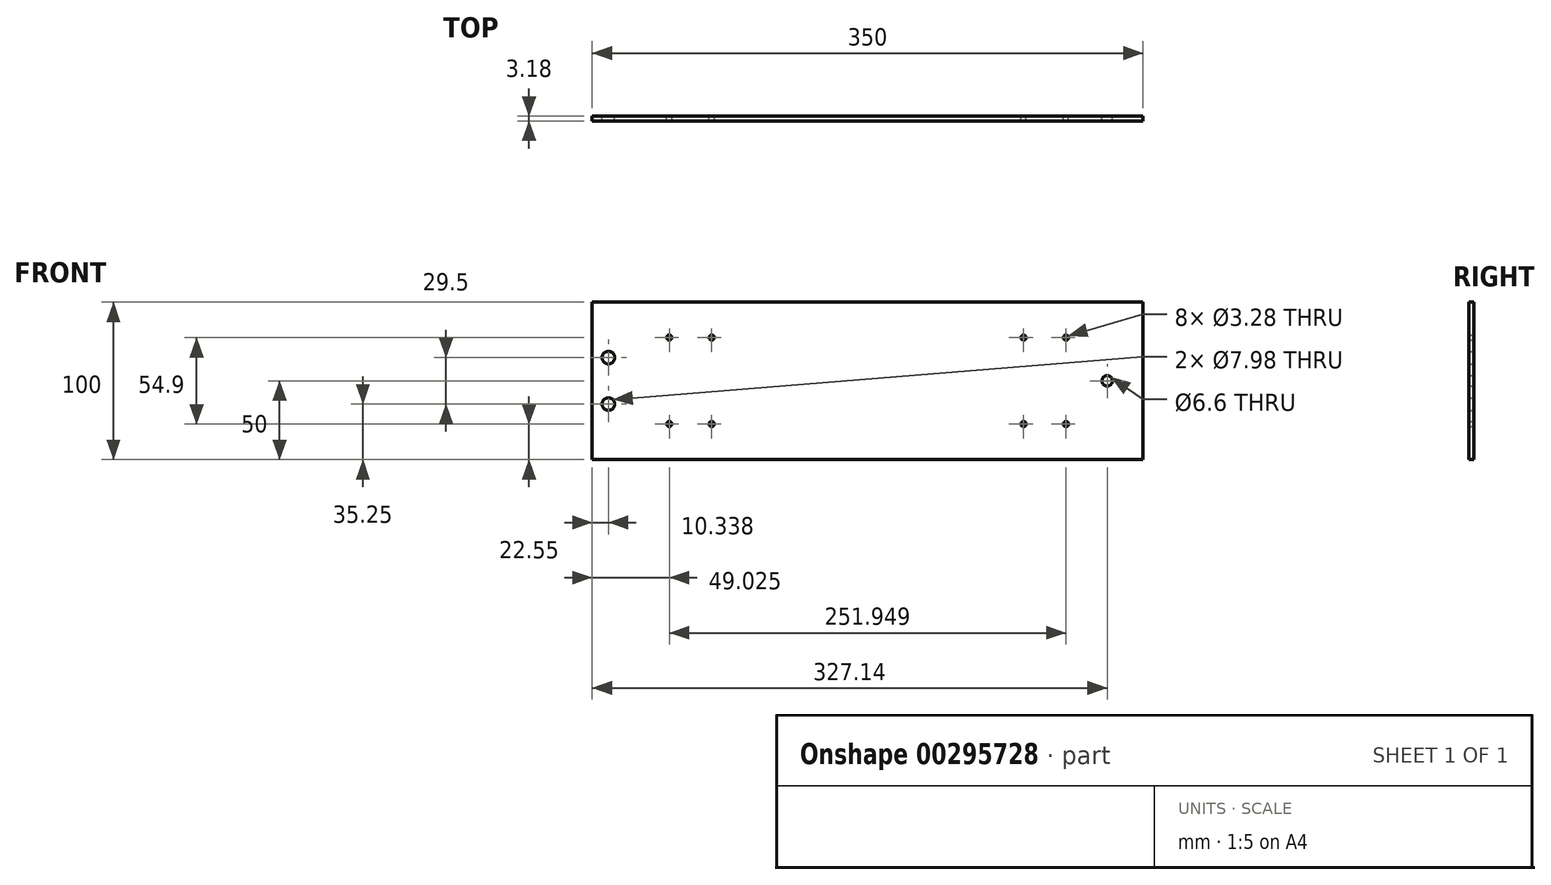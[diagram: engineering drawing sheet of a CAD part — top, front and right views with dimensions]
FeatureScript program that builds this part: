
annotation { "Feature Type Name" : "Feature", "Feature Type Description" : "" }
export const myFeature = defineFeature(function(context is Context, id is Id, definition is map)
    precondition{}
    {
        {
            var Q0;
            Q0=qCreatedBy(makeId("Front.planeOp"),FACE);
            var sketch = newSketch(context, id + "F0", { "sketchPlane" : qUnion([Q0])});
            skLineSegment(sketch, "E0.bottom", {"start": v(175, -75) * mm, "end": v(-175, -75) * mm});
            skLineSegment(sketch, "E0.top", {"start": v(175, 25) * mm, "end": v(-175, 25) * mm});
            skLineSegment(sketch, "E0.left", {"start": v(175, -75) * mm, "end": v(175, 25) * mm});
            skLineSegment(sketch, "E0.right", {"start": v(-175, -75) * mm, "end": v(-175, 25) * mm});
            skCircle(sketch, "E1", {"center": v(-112.5, 2.45) * mm, "radius": 4 * mm, "construction": true});
            skLineSegment(sketch, "E2", {"start": v(-112.5, 2.45) * mm, "end": v(-108.5, 2.45) * mm, "construction": true});
            skLineSegment(sketch, "E3", {"start": v(-112.5, 2.45) * mm, "end": v(-112.5, 6.45) * mm, "construction": true});
            skCircle(sketch, "E4", {"center": v(-99.03, 2.45) * mm, "radius": 1.64 * mm});
            skCircle(sketch, "E5.MirrorC", {"center": v(-125.97, 2.45) * mm, "radius": 1.64 * mm});
            skCircle(sketch, "E6", {"center": v(-112.5, -52.45) * mm, "radius": 4 * mm, "construction": true});
            skLineSegment(sketch, "E7", {"start": v(-112.5, -52.45) * mm, "end": v(-108.5, -52.45) * mm, "construction": true});
            skLineSegment(sketch, "E8", {"start": v(-112.5, -52.45) * mm, "end": v(-112.5, -48.45) * mm, "construction": true});
            skCircle(sketch, "E9", {"center": v(-99.03, -52.45) * mm, "radius": 1.64 * mm});
            skCircle(sketch, "E10.MirrorC", {"center": v(-125.97, -52.45) * mm, "radius": 1.64 * mm});
            skCircle(sketch, "E11", {"center": v(112.5, -52.45) * mm, "radius": 4 * mm, "construction": true});
            skLineSegment(sketch, "E12", {"start": v(112.5, -52.45) * mm, "end": v(116.5, -52.45) * mm, "construction": true});
            skLineSegment(sketch, "E13", {"start": v(112.5, -52.45) * mm, "end": v(112.5, -48.45) * mm, "construction": true});
            skCircle(sketch, "E14", {"center": v(125.97, -52.45) * mm, "radius": 1.64 * mm});
            skCircle(sketch, "E15.MirrorC", {"center": v(99.03, -52.45) * mm, "radius": 1.64 * mm});
            skCircle(sketch, "E16", {"center": v(112.5, 2.45) * mm, "radius": 4 * mm, "construction": true});
            skLineSegment(sketch, "E17", {"start": v(112.5, 2.45) * mm, "end": v(116.5, 2.45) * mm, "construction": true});
            skLineSegment(sketch, "E18", {"start": v(112.5, 2.45) * mm, "end": v(112.5, 6.45) * mm, "construction": true});
            skCircle(sketch, "E19", {"center": v(125.97, 2.45) * mm, "radius": 1.64 * mm});
            skCircle(sketch, "E20.MirrorC", {"center": v(99.03, 2.45) * mm, "radius": 1.64 * mm});
            skLineSegment(sketch, "E21.bottom", {"start": v(-74.4, -81.35) * mm, "end": v(-150.6, -81.35) * mm, "construction": true});
            skLineSegment(sketch, "E21.top", {"start": v(-74.4, -75) * mm, "end": v(-150.6, -75) * mm, "construction": true});
            skLineSegment(sketch, "E21.left", {"start": v(-74.4, -81.35) * mm, "end": v(-74.4, -75) * mm, "construction": true});
            skLineSegment(sketch, "E21.right", {"start": v(-150.6, -81.35) * mm, "end": v(-150.6, -75) * mm, "construction": true});
            skPoint(sketch, "E21.middle", {"position": v(-112.5, -78.17) * mm});
            skPoint(sketch, "E21.middle.positionSnap0", {"position": v(-112.5, -50.45) * mm});
            skPoint(sketch, "E21.centerSnap0", {"position": v(-112.5, -50.45) * mm});
            skLineSegment(sketch, "E22.bottom", {"start": v(-74.4, -75) * mm, "end": v(-49, -75) * mm, "construction": true});
            skLineSegment(sketch, "E22.top", {"start": v(-74.4, -81.35) * mm, "end": v(-49, -81.35) * mm, "construction": true});
            skLineSegment(sketch, "E22.left", {"start": v(-74.4, -75) * mm, "end": v(-74.4, -81.35) * mm, "construction": true});
            skLineSegment(sketch, "E22.right", {"start": v(-49, -75) * mm, "end": v(-49, -81.35) * mm, "construction": true});
            skLineSegment(sketch, "E23", {"start": v(-61.7, -75) * mm, "end": v(-61.7, -81.35) * mm, "construction": true});
            skLineSegment(sketch, "E24.MirrorCS", {"start": v(-74.4, 75) * mm, "end": v(-49, 75) * mm, "construction": true});
            skPoint(sketch, "E25.endSnap0", {"position": v(112.5, 0) * mm});
            skLineSegment(sketch, "E26.right", {"start": v(131.55, -7.94) * mm, "end": v(131.55, 7.94) * mm});
            skCircle(sketch, "E27", {"center": v(152.14, -25) * mm, "radius": 3.3 * mm});
            skCircle(sketch, "E28", {"center": v(-164.66, -39.75) * mm, "radius": 3.99 * mm});
            skLineSegment(sketch, "E29.bottom", {"start": v(-164.66, -39.75) * mm, "end": v(-125.97, -39.75) * mm, "construction": true});
            skLineSegment(sketch, "E29.top", {"start": v(-164.66, -52.45) * mm, "end": v(-125.97, -52.45) * mm, "construction": true});
            skLineSegment(sketch, "E29.left", {"start": v(-164.66, -39.75) * mm, "end": v(-164.66, -52.45) * mm, "construction": true});
            skLineSegment(sketch, "E29.right", {"start": v(-125.97, -39.75) * mm, "end": v(-125.97, -52.45) * mm, "construction": true});
            skLineSegment(sketch, "E30", {"start": v(0, 25) * mm, "end": v(0, -75) * mm, "construction": true});
            skLineSegment(sketch, "E31", {"start": v(0, -25) * mm, "end": v(-175, -25) * mm, "construction": true});
            skCircle(sketch, "E32.MirrorC", {"center": v(-164.66, -10.25) * mm, "radius": 3.99 * mm});
            skSolve(sketch);
        }
        {
            var Q0;
            Q0=qSketchRegion(id+"F0",true);
            extrude(context, id + "F1", {"entities" : qUnion([Q0]), "depth" : 3.17 * mm});
        }
    });
